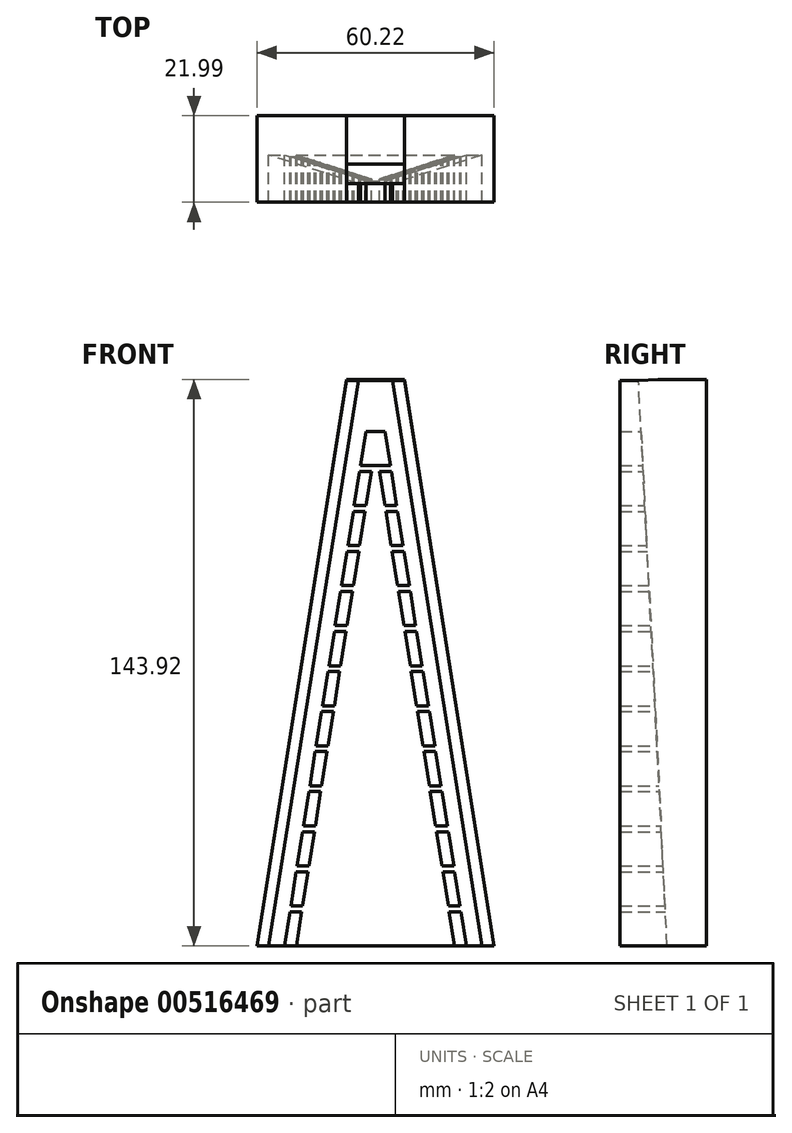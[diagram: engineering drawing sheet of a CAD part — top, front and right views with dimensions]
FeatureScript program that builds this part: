
annotation { "Feature Type Name" : "Feature", "Feature Type Description" : "" }
export const myFeature = defineFeature(function(context is Context, id is Id, definition is map)
    precondition{}
    {
        {
            var Q0;
            Q0=qCreatedBy(makeId("Front.planeOp"),FACE);
            var sketch = newSketch(context, id + "F0", { "sketchPlane" : qUnion([Q0])});
            skLineSegment(sketch, "E0", {"start": v(-21.74, 8.67) * mm, "end": v(-18.74, 8.67) * mm});
            skLineSegment(sketch, "E1", {"start": v(-18.74, 8.67) * mm, "end": v(-20.11, 0) * mm});
            skLineSegment(sketch, "E2", {"start": v(-20.11, 0) * mm, "end": v(-23.11, 0) * mm});
            skLineSegment(sketch, "E3", {"start": v(-23.11, 0) * mm, "end": v(-21.74, 8.67) * mm});
            skLineSegment(sketch, "E4", {"start": v(18.74, 8.67) * mm, "end": v(21.74, 8.67) * mm});
            skLineSegment(sketch, "E5", {"start": v(21.74, 8.67) * mm, "end": v(23.11, 0) * mm});
            skLineSegment(sketch, "E6", {"start": v(23.11, 0) * mm, "end": v(20.11, 0) * mm});
            skLineSegment(sketch, "E7", {"start": v(20.11, 0) * mm, "end": v(18.74, 8.67) * mm});
            skLineSegment(sketch, "E8", {"start": v(-21.5, 10.17) * mm, "end": v(-18.5, 10.17) * mm});
            skLineSegment(sketch, "E9", {"start": v(-18.5, 10.17) * mm, "end": v(-17.13, 18.83) * mm});
            skLineSegment(sketch, "E10", {"start": v(-17.13, 18.83) * mm, "end": v(-20.13, 18.83) * mm});
            skLineSegment(sketch, "E11", {"start": v(-20.13, 18.83) * mm, "end": v(-21.5, 10.17) * mm});
            skLineSegment(sketch, "E12", {"start": v(18.5, 10.17) * mm, "end": v(17.13, 18.83) * mm});
            skLineSegment(sketch, "E13", {"start": v(17.13, 18.83) * mm, "end": v(20.13, 18.83) * mm});
            skLineSegment(sketch, "E14", {"start": v(20.13, 18.83) * mm, "end": v(21.5, 10.17) * mm});
            skLineSegment(sketch, "E15", {"start": v(21.5, 10.17) * mm, "end": v(18.5, 10.17) * mm});
            skLineSegment(sketch, "E16", {"start": v(-18.52, 29) * mm, "end": v(-19.89, 20.33) * mm});
            skLineSegment(sketch, "E17", {"start": v(-19.89, 20.33) * mm, "end": v(-16.89, 20.33) * mm});
            skLineSegment(sketch, "E18", {"start": v(-16.89, 20.33) * mm, "end": v(-15.52, 29) * mm});
            skLineSegment(sketch, "E19", {"start": v(-15.52, 29) * mm, "end": v(-18.52, 29) * mm});
            skLineSegment(sketch, "E20", {"start": v(19.89, 20.33) * mm, "end": v(18.52, 29) * mm});
            skLineSegment(sketch, "E21", {"start": v(18.52, 29) * mm, "end": v(15.52, 29) * mm});
            skLineSegment(sketch, "E22", {"start": v(15.52, 29) * mm, "end": v(16.89, 20.33) * mm});
            skLineSegment(sketch, "E23", {"start": v(16.89, 20.33) * mm, "end": v(19.89, 20.33) * mm});
            skLineSegment(sketch, "E24", {"start": v(-16.67, 40.67) * mm, "end": v(-13.67, 40.67) * mm});
            skLineSegment(sketch, "E25", {"start": v(-13.67, 40.67) * mm, "end": v(-12.3, 49.33) * mm});
            skLineSegment(sketch, "E26", {"start": v(-12.3, 49.33) * mm, "end": v(-15.3, 49.33) * mm});
            skLineSegment(sketch, "E27", {"start": v(-15.3, 49.33) * mm, "end": v(-16.67, 40.67) * mm});
            skLineSegment(sketch, "E28", {"start": v(-13.69, 59.5) * mm, "end": v(-15.06, 50.83) * mm});
            skLineSegment(sketch, "E29", {"start": v(-8.84, 71.17) * mm, "end": v(-11.84, 71.17) * mm});
            skLineSegment(sketch, "E30", {"start": v(-7.47, 79.83) * mm, "end": v(-10.47, 79.83) * mm});
            skLineSegment(sketch, "E31", {"start": v(-10.47, 79.83) * mm, "end": v(-11.84, 71.17) * mm});
            skLineSegment(sketch, "E32", {"start": v(-8.86, 90) * mm, "end": v(-10.23, 81.33) * mm});
            skLineSegment(sketch, "E33", {"start": v(-10.23, 81.33) * mm, "end": v(-7.23, 81.33) * mm});
            skLineSegment(sketch, "E34", {"start": v(-7.23, 81.33) * mm, "end": v(-5.86, 90) * mm});
            skLineSegment(sketch, "E35", {"start": v(-5.86, 90) * mm, "end": v(-8.86, 90) * mm});
            skLineSegment(sketch, "E36", {"start": v(-7.25, 100.17) * mm, "end": v(-8.62, 91.5) * mm});
            skLineSegment(sketch, "E37", {"start": v(-8.62, 91.5) * mm, "end": v(-5.62, 91.5) * mm});
            skLineSegment(sketch, "E38", {"start": v(-5.62, 91.5) * mm, "end": v(-4.25, 100.17) * mm});
            skLineSegment(sketch, "E39", {"start": v(-7.25, 100.17) * mm, "end": v(-4.25, 100.17) * mm});
            skLineSegment(sketch, "E40", {"start": v(13.9, 39.17) * mm, "end": v(16.9, 39.17) * mm});
            skLineSegment(sketch, "E41", {"start": v(16.9, 39.17) * mm, "end": v(18.28, 30.5) * mm});
            skLineSegment(sketch, "E42", {"start": v(18.28, 30.5) * mm, "end": v(15.28, 30.5) * mm});
            skLineSegment(sketch, "E43", {"start": v(15.28, 30.5) * mm, "end": v(13.9, 39.17) * mm});
            skLineSegment(sketch, "E44", {"start": v(12.3, 49.33) * mm, "end": v(15.3, 49.33) * mm});
            skLineSegment(sketch, "E45", {"start": v(15.3, 49.33) * mm, "end": v(16.67, 40.67) * mm});
            skLineSegment(sketch, "E46", {"start": v(16.67, 40.67) * mm, "end": v(13.67, 40.67) * mm});
            skLineSegment(sketch, "E47", {"start": v(13.67, 40.67) * mm, "end": v(12.3, 49.33) * mm});
            skLineSegment(sketch, "E48", {"start": v(10.69, 59.5) * mm, "end": v(13.69, 59.5) * mm});
            skLineSegment(sketch, "E49", {"start": v(13.69, 59.5) * mm, "end": v(15.06, 50.83) * mm});
            skLineSegment(sketch, "E50", {"start": v(15.06, 50.83) * mm, "end": v(12.06, 50.83) * mm});
            skLineSegment(sketch, "E51", {"start": v(12.06, 50.83) * mm, "end": v(10.69, 59.5) * mm});
            skLineSegment(sketch, "E52", {"start": v(13.45, 61) * mm, "end": v(10.45, 61) * mm});
            skLineSegment(sketch, "E53", {"start": v(7.47, 79.83) * mm, "end": v(10.47, 79.83) * mm});
            skLineSegment(sketch, "E54", {"start": v(10.47, 79.83) * mm, "end": v(11.84, 71.17) * mm});
            skLineSegment(sketch, "E55", {"start": v(11.84, 71.17) * mm, "end": v(8.84, 71.17) * mm});
            skLineSegment(sketch, "E56", {"start": v(8.84, 71.17) * mm, "end": v(7.47, 79.83) * mm});
            skLineSegment(sketch, "E57", {"start": v(5.86, 90) * mm, "end": v(8.86, 90) * mm});
            skLineSegment(sketch, "E58", {"start": v(8.86, 90) * mm, "end": v(10.23, 81.33) * mm});
            skLineSegment(sketch, "E59", {"start": v(10.23, 81.33) * mm, "end": v(7.23, 81.33) * mm});
            skLineSegment(sketch, "E60", {"start": v(7.23, 81.33) * mm, "end": v(5.86, 90) * mm});
            skLineSegment(sketch, "E61", {"start": v(-23.11, 192.36) * mm, "end": v(-23.11, -60.17) * mm, "construction": true});
            skLineSegment(sketch, "E62", {"start": v(-16.9, 39.17) * mm, "end": v(-18.28, 30.5) * mm});
            skLineSegment(sketch, "E63", {"start": v(-18.28, 30.5) * mm, "end": v(-15.28, 30.5) * mm});
            skLineSegment(sketch, "E64", {"start": v(-15.28, 30.5) * mm, "end": v(-13.9, 39.17) * mm});
            skLineSegment(sketch, "E65", {"start": v(-13.9, 39.17) * mm, "end": v(-16.9, 39.17) * mm});
            skLineSegment(sketch, "E66", {"start": v(23.11, 282.2) * mm, "end": v(23.11, 74.17) * mm, "construction": true});
            skLineSegment(sketch, "E67", {"start": v(-18.5, 10.17) * mm, "end": v(18.5, 10.17) * mm, "construction": true});
            skLineSegment(sketch, "E68", {"start": v(-20.11, 0) * mm, "end": v(20.11, 0) * mm, "construction": true});
            skLineSegment(sketch, "E69", {"start": v(-18.74, 8.67) * mm, "end": v(18.74, 8.67) * mm, "construction": true});
            skLineSegment(sketch, "E70", {"start": v(-17.13, 18.83) * mm, "end": v(17.13, 18.83) * mm, "construction": true});
            skLineSegment(sketch, "E71", {"start": v(-16.89, 20.33) * mm, "end": v(16.89, 20.33) * mm, "construction": true});
            skLineSegment(sketch, "E72", {"start": v(-15.52, 29) * mm, "end": v(15.52, 29) * mm, "construction": true});
            skLineSegment(sketch, "E73", {"start": v(-15.28, 30.5) * mm, "end": v(15.28, 30.5) * mm, "construction": true});
            skLineSegment(sketch, "E74", {"start": v(-13.9, 39.17) * mm, "end": v(13.9, 39.17) * mm, "construction": true});
            skLineSegment(sketch, "E75", {"start": v(-13.67, 40.67) * mm, "end": v(13.67, 40.67) * mm, "construction": true});
            skLineSegment(sketch, "E76", {"start": v(-12.3, 49.33) * mm, "end": v(12.3, 49.33) * mm, "construction": true});
            skLineSegment(sketch, "E77", {"start": v(-7.47, 79.83) * mm, "end": v(7.47, 79.83) * mm, "construction": true});
            skLineSegment(sketch, "E78", {"start": v(-7.23, 81.33) * mm, "end": v(7.23, 81.33) * mm, "construction": true});
            skLineSegment(sketch, "E79", {"start": v(-5.86, 90) * mm, "end": v(5.86, 90) * mm, "construction": true});
            skLineSegment(sketch, "E80", {"start": v(-5.62, 91.5) * mm, "end": v(5.62, 91.5) * mm, "construction": true});
            skLineSegment(sketch, "E81", {"start": v(-4.25, 100.17) * mm, "end": v(4.25, 100.17) * mm, "construction": true});
            skLineSegment(sketch, "E82", {"start": v(-21.74, 8.67) * mm, "end": v(-21.5, 10.17) * mm, "construction": true});
            skLineSegment(sketch, "E83", {"start": v(-20.13, 18.83) * mm, "end": v(-19.89, 20.33) * mm, "construction": true});
            skLineSegment(sketch, "E84", {"start": v(-18.52, 29) * mm, "end": v(-18.28, 30.5) * mm, "construction": true});
            skLineSegment(sketch, "E85", {"start": v(-16.9, 39.17) * mm, "end": v(-16.67, 40.67) * mm, "construction": true});
            skLineSegment(sketch, "E86", {"start": v(-15.3, 49.33) * mm, "end": v(-15.06, 50.83) * mm, "construction": true});
            skLineSegment(sketch, "E87", {"start": v(-13.69, 59.5) * mm, "end": v(-13.45, 61) * mm, "construction": true});
            skLineSegment(sketch, "E88", {"start": v(-11.84, 71.17) * mm, "end": v(-11.84, 71.17) * mm});
            skLineSegment(sketch, "E89", {"start": v(-10.23, 81.33) * mm, "end": v(-10.47, 79.83) * mm, "construction": true});
            skLineSegment(sketch, "E90", {"start": v(-8.86, 90) * mm, "end": v(-8.62, 91.5) * mm, "construction": true});
            skLineSegment(sketch, "E91", {"start": v(-13.69, 59.5) * mm, "end": v(-10.69, 59.5) * mm});
            skLineSegment(sketch, "E92", {"start": v(-10.69, 59.5) * mm, "end": v(-12.06, 50.83) * mm});
            skLineSegment(sketch, "E93", {"start": v(-12.06, 50.83) * mm, "end": v(-15.06, 50.83) * mm});
            skLineSegment(sketch, "E94", {"start": v(-10.69, 59.5) * mm, "end": v(10.69, 59.5) * mm, "construction": true});
            skLineSegment(sketch, "E95", {"start": v(-12.06, 50.83) * mm, "end": v(12.06, 50.83) * mm, "construction": true});
            skLineSegment(sketch, "E96", {"start": v(-18.74, 8.67) * mm, "end": v(-18.5, 10.17) * mm, "construction": true});
            skLineSegment(sketch, "E97", {"start": v(-17.13, 18.83) * mm, "end": v(-16.89, 20.33) * mm, "construction": true});
            skLineSegment(sketch, "E98", {"start": v(-15.52, 29) * mm, "end": v(-15.28, 30.5) * mm, "construction": true});
            skLineSegment(sketch, "E99", {"start": v(-13.9, 39.17) * mm, "end": v(-13.67, 40.67) * mm, "construction": true});
            skLineSegment(sketch, "E100", {"start": v(-12.3, 49.33) * mm, "end": v(-12.06, 50.83) * mm, "construction": true});
            skLineSegment(sketch, "E101", {"start": v(-8.84, 71.17) * mm, "end": v(8.84, 71.17) * mm, "construction": true});
            skLineSegment(sketch, "E102", {"start": v(-13.45, 61) * mm, "end": v(-12.08, 69.67) * mm});
            skLineSegment(sketch, "E103", {"start": v(13.45, 61) * mm, "end": v(12.08, 69.67) * mm});
            skLineSegment(sketch, "E104", {"start": v(12.08, 69.67) * mm, "end": v(9.08, 69.67) * mm});
            skLineSegment(sketch, "E105", {"start": v(9.08, 69.67) * mm, "end": v(10.45, 61) * mm});
            skLineSegment(sketch, "E106", {"start": v(-7.47, 79.83) * mm, "end": v(-7.23, 81.33) * mm, "construction": true});
            skLineSegment(sketch, "E107", {"start": v(-5.86, 90) * mm, "end": v(-5.62, 91.5) * mm, "construction": true});
            skLineSegment(sketch, "E108", {"start": v(-12.08, 69.67) * mm, "end": v(-9.08, 69.67) * mm});
            skLineSegment(sketch, "E109", {"start": v(-9.08, 69.67) * mm, "end": v(-10.45, 61) * mm});
            skLineSegment(sketch, "E110", {"start": v(-10.45, 61) * mm, "end": v(-13.45, 61) * mm});
            skLineSegment(sketch, "E111", {"start": v(-12.08, 69.67) * mm, "end": v(-11.84, 71.17) * mm, "construction": true});
            skLineSegment(sketch, "E112", {"start": v(-8.84, 71.17) * mm, "end": v(-9.08, 69.67) * mm, "construction": true});
            skLineSegment(sketch, "E113", {"start": v(-10.45, 61) * mm, "end": v(-10.69, 59.5) * mm, "construction": true});
            skLineSegment(sketch, "E114", {"start": v(-7.47, 79.83) * mm, "end": v(-8.84, 71.17) * mm});
            skLineSegment(sketch, "E115", {"start": v(-9.08, 69.67) * mm, "end": v(9.08, 69.67) * mm, "construction": true});
            skLineSegment(sketch, "E116", {"start": v(-10.45, 61) * mm, "end": v(10.45, 61) * mm, "construction": true});
            skLineSegment(sketch, "E117", {"start": v(15.52, 29) * mm, "end": v(15.28, 30.5) * mm, "construction": true});
            skLineSegment(sketch, "E118", {"start": v(18.28, 30.5) * mm, "end": v(18.52, 29) * mm, "construction": true});
            skLineSegment(sketch, "E119", {"start": v(16.67, 40.67) * mm, "end": v(16.9, 39.17) * mm, "construction": true});
            skLineSegment(sketch, "E120", {"start": v(13.67, 40.67) * mm, "end": v(13.9, 39.17) * mm, "construction": true});
            skLineSegment(sketch, "E121", {"start": v(20.13, 18.83) * mm, "end": v(19.89, 20.33) * mm, "construction": true});
            skLineSegment(sketch, "E122", {"start": v(17.13, 18.83) * mm, "end": v(16.89, 20.33) * mm, "construction": true});
            skLineSegment(sketch, "E123", {"start": v(10.23, 81.33) * mm, "end": v(10.47, 79.83) * mm, "construction": true});
            skLineSegment(sketch, "E124", {"start": v(12.08, 69.67) * mm, "end": v(11.84, 71.17) * mm, "construction": true});
            skLineSegment(sketch, "E125", {"start": v(13.45, 61) * mm, "end": v(13.69, 59.5) * mm, "construction": true});
            skLineSegment(sketch, "E126", {"start": v(10.69, 59.5) * mm, "end": v(10.45, 61) * mm, "construction": true});
            skLineSegment(sketch, "E127", {"start": v(9.08, 69.67) * mm, "end": v(8.84, 71.17) * mm, "construction": true});
            skLineSegment(sketch, "E128", {"start": v(7.47, 79.83) * mm, "end": v(7.23, 81.33) * mm, "construction": true});
            skLineSegment(sketch, "E129", {"start": v(5.86, 90) * mm, "end": v(5.62, 91.5) * mm, "construction": true});
            skLineSegment(sketch, "E130", {"start": v(12.06, 50.83) * mm, "end": v(12.3, 49.33) * mm, "construction": true});
            skLineSegment(sketch, "E131", {"start": v(15.3, 49.33) * mm, "end": v(15.06, 50.83) * mm, "construction": true});
            skLineSegment(sketch, "E132", {"start": v(18.5, 10.17) * mm, "end": v(18.74, 8.67) * mm, "construction": true});
            skLineSegment(sketch, "E133", {"start": v(21.5, 10.17) * mm, "end": v(21.74, 8.67) * mm, "construction": true});
            skLineSegment(sketch, "E134", {"start": v(4.25, 100.17) * mm, "end": v(5.62, 91.5) * mm});
            skLineSegment(sketch, "E135", {"start": v(5.62, 91.5) * mm, "end": v(8.62, 91.5) * mm});
            skLineSegment(sketch, "E136", {"start": v(8.62, 91.5) * mm, "end": v(7.25, 100.17) * mm});
            skLineSegment(sketch, "E137", {"start": v(7.25, 100.17) * mm, "end": v(4.25, 100.17) * mm});
            skLineSegment(sketch, "E138", {"start": v(8.62, 91.5) * mm, "end": v(8.86, 90) * mm, "construction": true});
            skLineSegment(sketch, "E139", {"start": v(27.82, 100.17) * mm, "end": v(27.82, 91.5) * mm, "construction": true});
            skLineSegment(sketch, "E140", {"start": v(16.69, 90) * mm, "end": v(16.69, 81.33) * mm, "construction": true});
            skLineSegment(sketch, "E141", {"start": v(15.77, 79.83) * mm, "end": v(15.77, 71.17) * mm, "construction": true});
            skLineSegment(sketch, "E142", {"start": v(14.86, 69.67) * mm, "end": v(14.86, 61) * mm, "construction": true});
            skLineSegment(sketch, "E143", {"start": v(10.43, 59.5) * mm, "end": v(10.43, 50.83) * mm, "construction": true});
            skLineSegment(sketch, "E144", {"start": v(9.82, 49.33) * mm, "end": v(9.82, 40.67) * mm, "construction": true});
            skLineSegment(sketch, "E145", {"start": v(9.06, 39.17) * mm, "end": v(9.06, 30.5) * mm, "construction": true});
            skLineSegment(sketch, "E146", {"start": v(7.38, 29) * mm, "end": v(7.38, 20.33) * mm, "construction": true});
            skLineSegment(sketch, "E147", {"start": v(9.21, 18.83) * mm, "end": v(9.21, 10.17) * mm, "construction": true});
            skLineSegment(sketch, "E148", {"start": v(-201.28, 8.67) * mm, "end": v(-201.28, 0) * mm, "construction": true});
            skLineSegment(sketch, "E149", {"start": v(104.46, 8.67) * mm, "end": v(104.46, 10.17) * mm, "construction": true});
            skLineSegment(sketch, "E150", {"start": v(102.28, 18.83) * mm, "end": v(102.28, 20.33) * mm, "construction": true});
            skLineSegment(sketch, "E151", {"start": v(106.09, 29) * mm, "end": v(106.09, 30.5) * mm, "construction": true});
            skLineSegment(sketch, "E152", {"start": v(98.47, 39.17) * mm, "end": v(98.47, 40.67) * mm, "construction": true});
            skLineSegment(sketch, "E153", {"start": v(104.46, 49.33) * mm, "end": v(104.46, 50.83) * mm, "construction": true});
            skLineSegment(sketch, "E154", {"start": v(94.3, 59.5) * mm, "end": v(94.3, 61) * mm, "construction": true});
            skLineSegment(sketch, "E155", {"start": v(102.64, 69.67) * mm, "end": v(102.64, 71.17) * mm, "construction": true});
            skLineSegment(sketch, "E156", {"start": v(87.4, 79.83) * mm, "end": v(87.4, 81.33) * mm, "construction": true});
            skLineSegment(sketch, "E157", {"start": v(98.1, 90) * mm, "end": v(98.1, 91.5) * mm, "construction": true});
            skLineSegment(sketch, "E158", {"start": v(-6.41, 130.67) * mm, "end": v(-27.11, 0) * mm});
            skLineSegment(sketch, "E159", {"start": v(-27.11, 0) * mm, "end": v(-30.11, 0) * mm});
            skLineSegment(sketch, "E160", {"start": v(-30.11, 0) * mm, "end": v(-9.41, 130.67) * mm});
            skLineSegment(sketch, "E161", {"start": v(-9.41, 130.67) * mm, "end": v(-6.41, 130.67) * mm});
            skLineSegment(sketch, "E162", {"start": v(6.41, 130.67) * mm, "end": v(9.41, 130.67) * mm});
            skLineSegment(sketch, "E163", {"start": v(9.41, 130.67) * mm, "end": v(30.11, 0) * mm});
            skLineSegment(sketch, "E164", {"start": v(30.11, 0) * mm, "end": v(27.11, 0) * mm});
            skLineSegment(sketch, "E165", {"start": v(27.11, 0) * mm, "end": v(6.41, 130.67) * mm});
            skLineSegment(sketch, "E166", {"start": v(-27.11, 0) * mm, "end": v(-23.11, 0) * mm, "construction": true});
            skLineSegment(sketch, "E167", {"start": v(23.11, 0) * mm, "end": v(27.11, 0) * mm, "construction": true});
            skLineSegment(sketch, "E168", {"start": v(-7, 101.67) * mm, "end": v(-4, 101.67) * mm});
            skLineSegment(sketch, "E169", {"start": v(-4, 101.67) * mm, "end": v(-2.64, 110.33) * mm});
            skLineSegment(sketch, "E170", {"start": v(-2.64, 110.33) * mm, "end": v(-5.64, 110.33) * mm});
            skLineSegment(sketch, "E171", {"start": v(-5.64, 110.33) * mm, "end": v(-7, 101.67) * mm});
            skLineSegment(sketch, "E172", {"start": v(2.64, 110.33) * mm, "end": v(5.64, 110.33) * mm});
            skLineSegment(sketch, "E173", {"start": v(5.64, 110.33) * mm, "end": v(7, 101.67) * mm});
            skLineSegment(sketch, "E174", {"start": v(7, 101.67) * mm, "end": v(4, 101.67) * mm});
            skLineSegment(sketch, "E175", {"start": v(4, 101.67) * mm, "end": v(2.64, 110.33) * mm});
            skLineSegment(sketch, "E176", {"start": v(-4, 101.67) * mm, "end": v(4, 101.67) * mm, "construction": true});
            skLineSegment(sketch, "E177", {"start": v(-2.64, 110.33) * mm, "end": v(2.64, 110.33) * mm, "construction": true});
            skLineSegment(sketch, "E178", {"start": v(0, 110.33) * mm, "end": v(0, 101.67) * mm, "construction": true});
            skLineSegment(sketch, "E179", {"start": v(0.52, 101.67) * mm, "end": v(0.52, 100.17) * mm, "construction": true});
            skLineSegment(sketch, "E180", {"start": v(-7.25, 100.17) * mm, "end": v(-7, 101.67) * mm, "construction": true});
            skLineSegment(sketch, "E181", {"start": v(7, 101.67) * mm, "end": v(7.25, 100.17) * mm, "construction": true});
            skLineSegment(sketch, "E182", {"start": v(4.25, 100.17) * mm, "end": v(4, 101.67) * mm, "construction": true});
            skLineSegment(sketch, "E183", {"start": v(-5.4, 111.83) * mm, "end": v(-2.4, 111.83) * mm});
            skLineSegment(sketch, "E184", {"start": v(-2.4, 111.83) * mm, "end": v(-1.02, 120.5) * mm});
            skLineSegment(sketch, "E185", {"start": v(-1.02, 120.5) * mm, "end": v(-4.02, 120.5) * mm});
            skLineSegment(sketch, "E186", {"start": v(-4.02, 120.5) * mm, "end": v(-5.4, 111.83) * mm});
            skLineSegment(sketch, "E187", {"start": v(1.02, 120.5) * mm, "end": v(4.02, 120.5) * mm});
            skLineSegment(sketch, "E188", {"start": v(4.02, 120.5) * mm, "end": v(5.4, 111.83) * mm});
            skLineSegment(sketch, "E189", {"start": v(5.4, 111.83) * mm, "end": v(2.4, 111.83) * mm});
            skLineSegment(sketch, "E190", {"start": v(2.4, 111.83) * mm, "end": v(1.02, 120.5) * mm});
            skLineSegment(sketch, "E191", {"start": v(-2.4, 111.83) * mm, "end": v(2.4, 111.83) * mm, "construction": true});
            skLineSegment(sketch, "E192", {"start": v(-1.02, 120.5) * mm, "end": v(1.02, 120.5) * mm, "construction": true});
            skLineSegment(sketch, "E193", {"start": v(0, 120.5) * mm, "end": v(0, 111.83) * mm, "construction": true});
            skLineSegment(sketch, "E194", {"start": v(5.4, 111.83) * mm, "end": v(5.64, 110.33) * mm, "construction": true});
            skLineSegment(sketch, "E195", {"start": v(0.6, 111.83) * mm, "end": v(0.6, 110.33) * mm, "construction": true});
            skLineSegment(sketch, "E196", {"start": v(2.64, 110.33) * mm, "end": v(2.4, 111.83) * mm, "construction": true});
            skLineSegment(sketch, "E197", {"start": v(-2.64, 110.33) * mm, "end": v(-2.4, 111.83) * mm, "construction": true});
            skLineSegment(sketch, "E198", {"start": v(-5.64, 110.33) * mm, "end": v(-5.4, 111.83) * mm, "construction": true});
            skLineSegment(sketch, "E199", {"start": v(-2.41, 130.67) * mm, "end": v(-3.79, 122) * mm});
            skLineSegment(sketch, "E200", {"start": v(2.41, 130.67) * mm, "end": v(3.79, 122) * mm});
            skLineSegment(sketch, "E201", {"start": v(4.02, 120.5) * mm, "end": v(3.79, 122) * mm, "construction": true});
            skLineSegment(sketch, "E202", {"start": v(-4.02, 120.5) * mm, "end": v(-3.79, 122) * mm, "construction": true});
            skLineSegment(sketch, "E203", {"start": v(-3.79, 122) * mm, "end": v(3.79, 122) * mm});
            skLineSegment(sketch, "E204", {"start": v(-2.41, 130.67) * mm, "end": v(2.41, 130.67) * mm});
            skLineSegment(sketch, "E205", {"start": v(0, 130.67) * mm, "end": v(0, 122) * mm, "construction": true});
            skLineSegment(sketch, "E206", {"start": v(0.43, 122) * mm, "end": v(0.43, 120.5) * mm, "construction": true});
            skLineSegment(sketch, "E207", {"start": v(-6.41, 130.67) * mm, "end": v(-2.41, 130.67) * mm, "construction": true});
            skLineSegment(sketch, "E208", {"start": v(6.41, 130.67) * mm, "end": v(2.41, 130.67) * mm, "construction": true});
            skLineSegment(sketch, "E209", {"start": v(-9.41, 130.67) * mm, "end": v(-7.36, 143.67) * mm});
            skLineSegment(sketch, "E210", {"start": v(-7.36, 143.67) * mm, "end": v(-4.36, 143.67) * mm});
            skLineSegment(sketch, "E211", {"start": v(-4.36, 143.67) * mm, "end": v(-6.41, 130.67) * mm});
            skLineSegment(sketch, "E212", {"start": v(6.41, 130.67) * mm, "end": v(4.36, 143.67) * mm});
            skLineSegment(sketch, "E213", {"start": v(4.36, 143.67) * mm, "end": v(7.36, 143.67) * mm});
            skLineSegment(sketch, "E214", {"start": v(7.36, 143.67) * mm, "end": v(9.41, 130.67) * mm});
            skLineSegment(sketch, "E215", {"start": v(-4.36, 143.67) * mm, "end": v(4.36, 143.67) * mm, "construction": true});
            skSolve(sketch);
        }
        {
            var Q0;
            Q0=qSketchRegion(id+"F0",true);
            extrude(context, id + "F1", {"entities" : qUnion([Q0]), "depth" : 12 * mm, "offsetDistance" : 25 * mm});
        }
        {
            var Q0;
            Q0=qCreatedBy(makeId("Right.planeOp"),FACE);
            var sketch = newSketch(context, id + "F2", { "sketchPlane" : qUnion([Q0])});
            skLineSegment(sketch, "E216", {"start": v(0, 0) * mm, "end": v(-7.28, 143.67) * mm});
            skLineSegment(sketch, "E217", {"start": v(-7.28, 143.67) * mm, "end": v(0, 143.67) * mm});
            skLineSegment(sketch, "E218", {"start": v(0, 143.67) * mm, "end": v(0, 0) * mm});
            skSolve(sketch);
        }
        {
            var Q0;
            Q0=qSketchRegion(id+"F2",true);
            extrude(context, id + "F3", {"entities" : qUnion([Q0]), "operationType" : NewBodyOperationType.REMOVE, "depth" : 80 * mm, "offsetDistance" : 25 * mm, "symmetric" : true});
        }
        {
            var Q0;
            Q0=makeQuery(id+"F3.boolean.opBoolean","COPY",FACE,{"disambiguationData":[TD([makeQuery(id+"F1.opExtrude","SWEPT_FACE",FACE,{"disambiguationData":[OSD([sQuery(id+"F0.wireOp",EDGE,"E164")])]})])],"derivedFrom":makeQuery(id+"F3.opExtrude","SWEPT_FACE",FACE,{"disambiguationData":[OSD([sQuery(id+"F2.wireOp",EDGE,"E216")])]})});
            var sketch = newSketch(context, id + "F4", { "sketchPlane" : qUnion([Q0])});
            skLineSegment(sketch, "E219", {"start": v(-7.36, 143.85) * mm, "end": v(7.36, 143.85) * mm});
            skLineSegment(sketch, "E220", {"start": v(7.36, 143.85) * mm, "end": v(30.11, 0) * mm});
            skLineSegment(sketch, "E221", {"start": v(30.11, 0) * mm, "end": v(-30.11, 0) * mm});
            skLineSegment(sketch, "E222", {"start": v(-30.11, 0) * mm, "end": v(-7.36, 143.85) * mm});
            skSolve(sketch);
        }
        {
            var Q0;
            Q0 = qSketchRegion(id + "F4", true);
            extrude(context, id + "F5", {"entities" : qUnion([Q0]), "operationType" : NewBodyOperationType.ADD, "depth" : 5 * mm, "offsetDistance" : 25 * mm});
        }
        {
            var Q0;
            Q0=qCreatedBy(makeId("Right.planeOp"),FACE);
            var sketch = newSketch(context, id + "F6", { "sketchPlane" : qUnion([Q0])});
            skLineSegment(sketch, "E223", {"start": v(-2.28, 143.92) * mm, "end": v(5, 0.25) * mm});
            skLineSegment(sketch, "E224", {"start": v(5, 0.25) * mm, "end": v(10, 0.25) * mm});
            skLineSegment(sketch, "E225", {"start": v(10, 0.25) * mm, "end": v(10, 143.92) * mm});
            skLineSegment(sketch, "E226", {"start": v(10, 143.92) * mm, "end": v(-2.28, 143.92) * mm});
            skSolve(sketch);
        }
        {
            var Q0;
            Q0 = qSketchRegion(id + "F6", true);
            extrude(context, id + "F7", {"entities" : qUnion([Q0]), "operationType" : NewBodyOperationType.ADD, "depth" : 62 * mm, "offsetDistance" : 25 * mm, "symmetric" : true});
        }
        {
            var Q0;
            Q0=qCreatedBy(makeId("Right.planeOp"),FACE);
            var sketch = newSketch(context, id + "F8", { "sketchPlane" : qUnion([Q0])});
            skLineSegment(sketch, "E227", {"start": v(5, 0.25) * mm, "end": v(0, 0) * mm});
            skLineSegment(sketch, "E228", {"start": v(0, 0) * mm, "end": v(10, 0) * mm});
            skLineSegment(sketch, "E229", {"start": v(10, 0) * mm, "end": v(10, 0.25) * mm});
            skLineSegment(sketch, "E230", {"start": v(10, 0.25) * mm, "end": v(5, 0.25) * mm});
            skSolve(sketch);
        }
        {
            var Q0;
            Q0 = qSketchRegion(id + "F8", true);
            extrude(context, id + "F9", {"entities" : qUnion([Q0]), "operationType" : NewBodyOperationType.ADD, "depth" : 63 * mm, "offsetDistance" : 25 * mm, "symmetric" : true});
        }
        {
            var Q0;
            Q0=qCreatedBy(makeId("Front.planeOp"),FACE);
            var sketch = newSketch(context, id + "F10", { "sketchPlane" : qUnion([Q0])});
            skLineSegment(sketch, "E231", {"start": v(31, 143.92) * mm, "end": v(31.5, 0) * mm});
            skLineSegment(sketch, "E232", {"start": v(31.5, 0) * mm, "end": v(30.11, 0) * mm});
            skLineSegment(sketch, "E233", {"start": v(30.11, 0) * mm, "end": v(7.36, 143.92) * mm});
            skLineSegment(sketch, "E234", {"start": v(7.36, 143.92) * mm, "end": v(31, 143.92) * mm});
            skLineSegment(sketch, "E235", {"start": v(-7.36, 143.92) * mm, "end": v(-30.11, 0) * mm});
            skLineSegment(sketch, "E236", {"start": v(-30.11, 0) * mm, "end": v(-31.5, 0) * mm});
            skLineSegment(sketch, "E237", {"start": v(-31.5, 0) * mm, "end": v(-31, 143.92) * mm});
            skLineSegment(sketch, "E238", {"start": v(-31, 143.92) * mm, "end": v(-7.36, 143.92) * mm});
            skSolve(sketch);
        }
        {
            var Q0;
            Q0 = qSketchRegion(id + "F10", true);
            extrude(context, id + "F11", {"entities" : qUnion([Q0]), "operationType" : NewBodyOperationType.REMOVE, "depth" : 30 * mm, "offsetDistance" : 25 * mm, "symmetric" : true});
        }
    });
